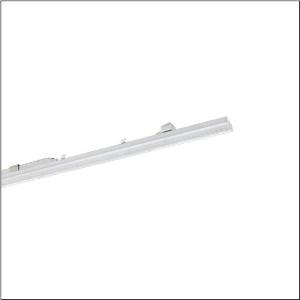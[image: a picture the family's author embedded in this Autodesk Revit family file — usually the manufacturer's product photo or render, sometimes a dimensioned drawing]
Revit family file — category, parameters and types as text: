
# Revit family: tl_l_5wd7a8f0a2b5
name_source: partatom
category: Lighting Fixtures
units: mm (PartAtom-declared; Revit-internal decimal feet)

## family parameters
Cut with Voids When Loaded = No
Host = Face
Light Source = No
Part Type = Normal
Room Calculation Point = No
Round Connector Dimension = Use Diameter
Shared = No

## types (1)
- TL L (1 x LED, 4990 lm, 30 W, 4000K)
    Apparent Load = 30 VA
    CIE Flux Codes = 49 84 98 100 100
    Color Rendering = 80
    Color Temperature = 4000K
    Default Elevation = 1800 mm
    Description = TL L, luminaire insert, of sheet steel, galvanised, coil coated, white, length: 1.500mm, width: 66mm, height: 67mm, LED rated luminous flux: 4.990lm, light colour: 840, control gear: 4..20mA, with terminal, 5-pole, mains connection: 230..240V, AC, 50/60Hz, rated input power: 30W, primary optical cover: cover, of PMMA, light emission: direct distribution, protection rating (complete): as luminaire, insulation class (complete): insulation class I (protective earthing), certification: CE, impact resistance: IK06, permissible ambient temperature for indoor applications: -25..+35°C, packaging unit: 1 piece
    Height = 120 mm
    Lamp = 1 x LED
    Lamp Light Flux = 4990 lm
    Lamp Power = 30 W
    Lamp count = 1
    Length = 1690 mm
    Luminous efficacy = 166 lm/W
    Manufacturer = Siteco
    ModVariant = No
    Model = 5WD7A8F0A2B5
    Mounting Place = Ceiling
    Mounting Type = Pendant
    Number of Poles = 1
    OnlyDefault = Yes
    Power Factor = 1
    Product Name = TL L
    Product group = luminaire insert
    ProductGroupID = 901
    Protection Class = Protection class I
    Protection Degree = Degree of protection
    RLX_Detail_Level = 1
    RLX_Emergency_Light_Flux = 0 lm
    RLX_Emergency_Type = 0
    RLX_Emergency_Type_DB = No
    RlxData = <blob elided: 14085 chars, md5=bd8f4018>
    Socket = socket
    Standby Power = 0 W
    System Light Flux = 4990 lm
    System Power = 30 W
    Type Comments = Product without accessories
    Type Image = l_1294382.jpg
    URL = http://relux.com
    VarID = ---
    Voltage = 0 V
    Weight = 0.00 kg
    Width = 208 mm

## geometry (parser evidence)
native form markers: Sweep x13
no freeform markers — native parametric forms only
